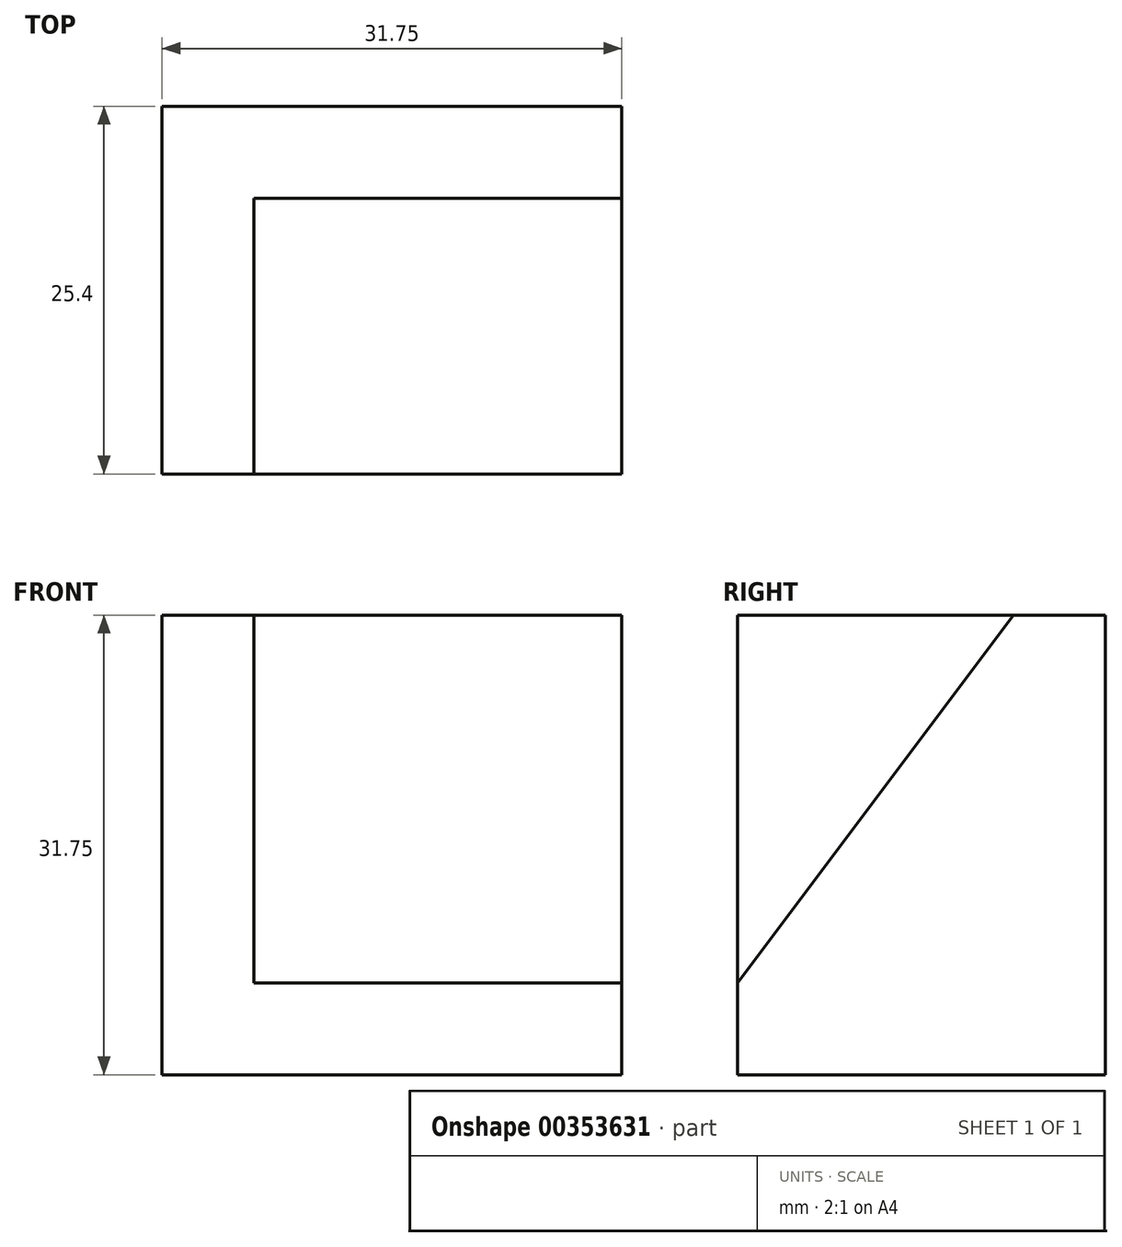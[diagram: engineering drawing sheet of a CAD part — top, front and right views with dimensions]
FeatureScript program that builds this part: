
annotation { "Feature Type Name" : "Feature", "Feature Type Description" : "" }
export const myFeature = defineFeature(function(context is Context, id is Id, definition is map)
    precondition{}
    {
        {
            var Q0;
            Q0=qCreatedBy(makeId("Front.planeOp"),FACE);
            var sketch = newSketch(context, id + "F0", { "sketchPlane" : qUnion([Q0])});
            skLineSegment(sketch, "E0", {"start": v(-29.61, 0) * mm, "end": v(-29.61, 31.75) * mm});
            skLineSegment(sketch, "E1", {"start": v(-29.61, 31.75) * mm, "end": v(8.49, 31.75) * mm});
            skLineSegment(sketch, "E2", {"start": v(8.49, 31.75) * mm, "end": v(8.49, 0) * mm});
            skLineSegment(sketch, "E3", {"start": v(8.49, 0) * mm, "end": v(-29.61, 0) * mm});
            skSolve(sketch);
        }
        {
            var Q0;
            Q0=makeQuery(id+"F0.imprint","IMPRINT",FACE,{"disambiguationData":[TD([[makeQuery(id+"F0.imprint","IMPRINT",EDGE,{"derivedFrom":sQuery(id+"F0.wireOp",EDGE,"E0")}),-1.0]])]});
            extrude(context, id + "F1", {"entities" : qUnion([Q0]), "depth" : 25.4 * mm});
        }
        {
            var Q0;
            Q0=makeQuery(id+"F1.opExtrude","SWEPT_FACE",FACE,{"disambiguationData":[OSD([sQuery(id+"F0.wireOp",EDGE,"E2")])]});
            var sketch = newSketch(context, id + "F2", { "sketchPlane" : qUnion([Q0])});
            skLineSegment(sketch, "E4", {"start": v(-25.4, 6.35) * mm, "end": v(-6.35, 31.75) * mm});
            skLineSegment(sketch, "E5", {"start": v(-6.35, 31.75) * mm, "end": v(0, 31.75) * mm});
            skLineSegment(sketch, "E6", {"start": v(0, 31.75) * mm, "end": v(0, 0) * mm});
            skLineSegment(sketch, "E7", {"start": v(0, 0) * mm, "end": v(-25.4, 0) * mm});
            skLineSegment(sketch, "E8", {"start": v(-25.4, 0) * mm, "end": v(-25.4, 6.35) * mm});
            skSolve(sketch);
        }
        {
            var Q0;
            Q0=makeQuery(id+"F2.imprint","IMPRINT",FACE,{"disambiguationData":[TD([[makeQuery(id+"F2.imprint","IMPRINT",EDGE,{"derivedFrom":sQuery(id+"F2.wireOp",EDGE,"E4")}),-1.0]])]});
            extrude(context, id + "F3", {"entities" : qUnion([Q0]), "operationType" : NewBodyOperationType.ADD, "depth" : 25.4 * mm});
        }
        {
            var Q0;
            Q0=makeQuery(id+"F1.opExtrude","SWEPT_FACE",FACE,{"disambiguationData":[OSD([sQuery(id+"F0.wireOp",EDGE,"E0")])]});
            var sketch = newSketch(context, id + "F4", { "sketchPlane" : qUnion([Q0])});
            skLineSegment(sketch, "E9", {"start": v(0, 31.75) * mm, "end": v(25.4, 31.75) * mm});
            skLineSegment(sketch, "E10", {"start": v(25.4, 31.75) * mm, "end": v(25.4, 0) * mm});
            skLineSegment(sketch, "E11", {"start": v(25.4, 0) * mm, "end": v(0, 0) * mm});
            skLineSegment(sketch, "E12", {"start": v(0, 0) * mm, "end": v(0, 31.75) * mm});
            skSolve(sketch);
        }
        {
            var Q0;
            Q0=makeQuery(id+"F4.imprint","IMPRINT",FACE,{"disambiguationData":[TD([[makeQuery(id+"F4.imprint","IMPRINT",EDGE,{"derivedFrom":sQuery(id+"F4.wireOp",EDGE,"E9")}),1.0]])]});
            extrude(context, id + "F5", {"entities" : qUnion([Q0]), "operationType" : NewBodyOperationType.REMOVE, "oppositeDirection" : true, "depth" : 31.75 * mm});
        }
        {
            var Q0;
            Q0=makeQuery(id+"F3.boolean.opBoolean","MERGE",FACE,{"derivedFrom":[makeQuery(id+"F1.opExtrude","CAP_FACE",FACE,{"disambiguationData":[OSD([sQuery(id+"F0.wireOp",EDGE,"E0"),sQuery(id+"F0.wireOp",EDGE,"E1"),sQuery(id+"F0.wireOp",EDGE,"E2"),sQuery(id+"F0.wireOp",EDGE,"E3")])],"isStart":false}),makeQuery(id+"F3.opExtrude","SWEPT_FACE",FACE,{"disambiguationData":[OSD([sQuery(id+"F2.wireOp",EDGE,"E8")])]})]});
            var sketch = newSketch(context, id + "F6", { "sketchPlane" : qUnion([Q0])});
            skLineSegment(sketch, "E13", {"start": v(0, 31.75) * mm, "end": v(0, 0) * mm});
            skLineSegment(sketch, "E14", {"start": v(0, 0) * mm, "end": v(-29.61, 0) * mm});
            skLineSegment(sketch, "E15", {"start": v(-29.61, 0) * mm, "end": v(-29.61, 31.75) * mm});
            skLineSegment(sketch, "E16", {"start": v(-29.61, 31.75) * mm, "end": v(0, 31.75) * mm});
            skSolve(sketch);
        }
        {
            var Q0;
            Q0=makeQuery(id+"F6.imprint","IMPRINT",FACE,{"disambiguationData":[TD([[makeQuery(id+"F6.imprint","IMPRINT",EDGE,{"derivedFrom":sQuery(id+"F6.wireOp",EDGE,"E13")}),-1.0]])]});
            extrude(context, id + "F7", {"entities" : qUnion([Q0]), "operationType" : NewBodyOperationType.REMOVE, "oppositeDirection" : true, "depth" : 25.4 * mm});
        }
    });
